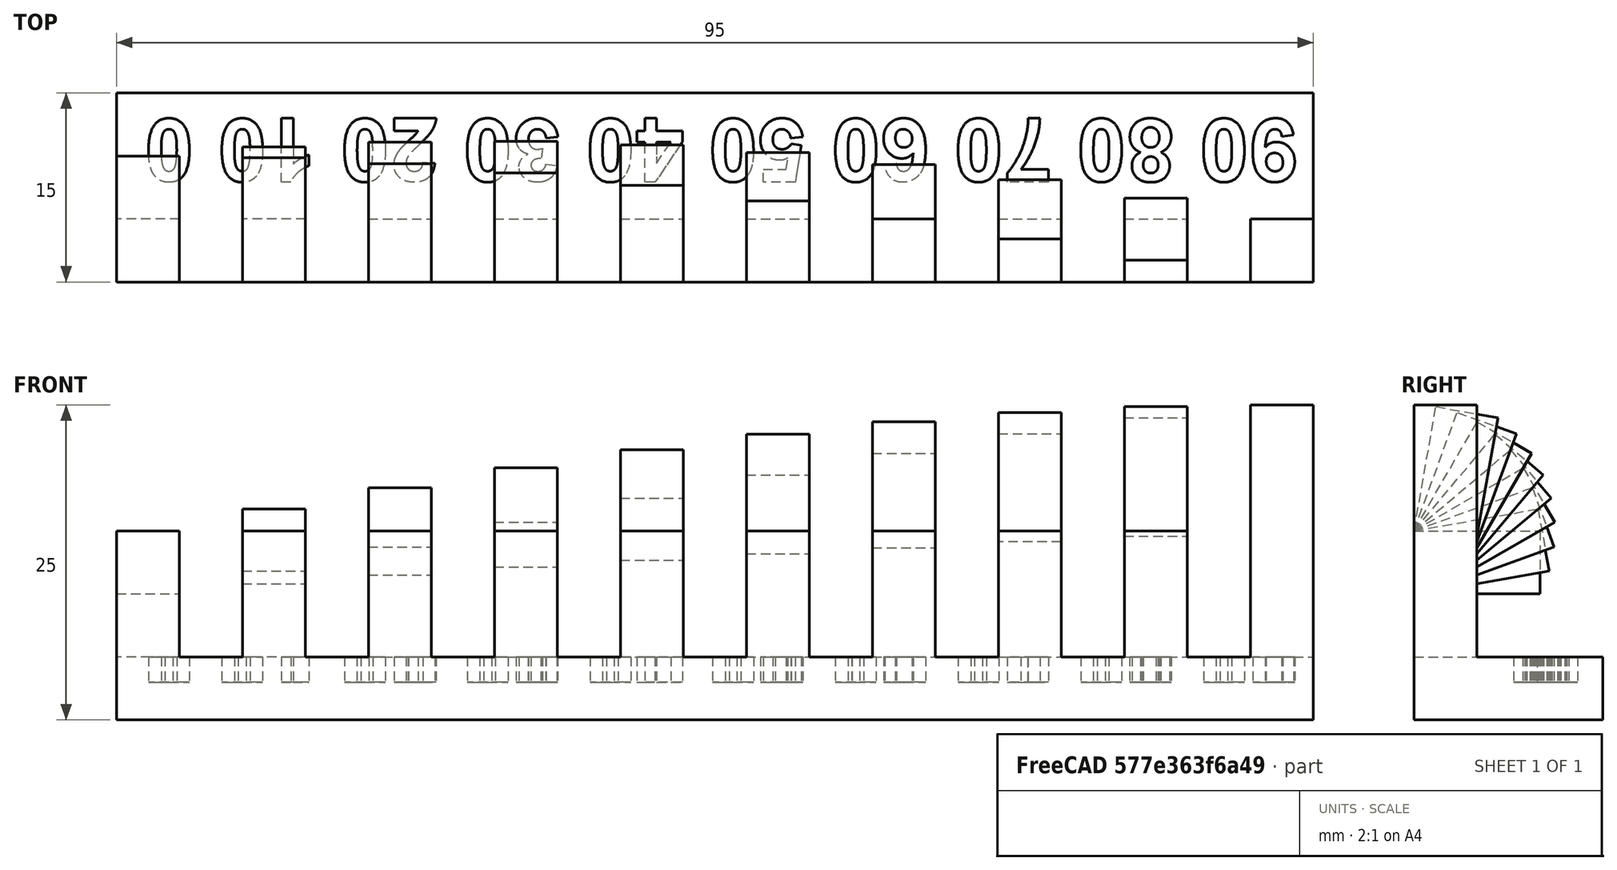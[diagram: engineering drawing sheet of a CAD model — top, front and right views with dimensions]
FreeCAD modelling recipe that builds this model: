
FCSTD DOCUMENT  (FreeCAD 0.18.3R)
Label: angle
License: All rights reserved
LicenseURL: http://en.wikipedia.org/wiki/All_rights_reserved
objects: Part::Box×20, Part::Fuse×8, Part::MultiFuse×2, Part::Part2DObjectPython×1, Part::Extrusion×1, Part::Cut×1
note: 33 computed .brp shape members not serialized (recipe doc carries the construction recipe); baked Part::Feature solids carry a one-line shape summary decoded from their .brp

FEATURE [Part::Box] Box  label="0"
  AttacherType = Attacher::AttachEngine3D
  Height = 20
  Length = 5
  Placement = pos=(0,0,-5) rot=(0,0,1;0rad)
  Width = 5
FEATURE [Part::Box] Box001  label="20 front"
  AttacherType = Attacher::AttachEngine3D
  Height = 10
  Length = 5
  Placement = pos=(-20,0,5) rot=(-1,0,0;0.349066rad)
  Width = 5
FEATURE [Part::Box] Box002  label="10 front"
  AttacherType = Attacher::AttachEngine3D
  Height = 10
  Length = 5
  Placement = pos=(-10,0,5) rot=(-1,0,0;0.174533rad)
  Width = 5
FEATURE [Part::Box] Box003  label="30 front"
  AttacherType = Attacher::AttachEngine3D
  Height = 10
  Length = 5
  Placement = pos=(-30,0,5) rot=(-1,0,0;0.523599rad)
  Width = 5
FEATURE [Part::Box] Box004  label="40 front"
  AttacherType = Attacher::AttachEngine3D
  Height = 10
  Length = 5
  Placement = pos=(-40,0,5) rot=(-1,0,0;0.698132rad)
  Width = 5
FEATURE [Part::Box] Box005  label="50 front"
  AttacherType = Attacher::AttachEngine3D
  Height = 10
  Length = 5
  Placement = pos=(-50,0,5) rot=(-1,0,0;0.872665rad)
  Width = 5
FEATURE [Part::Box] Box006  label="60 front"
  AttacherType = Attacher::AttachEngine3D
  Height = 10
  Length = 5
  Placement = pos=(-60,0,5) rot=(-1,0,0;1.0472rad)
  Width = 5
FEATURE [Part::Box] Box007  label="70 front"
  AttacherType = Attacher::AttachEngine3D
  Height = 10
  Length = 5
  Placement = pos=(-70,0,5) rot=(-1,0,0;1.22173rad)
  Width = 5
FEATURE [Part::Box] Box008  label="80 front"
  AttacherType = Attacher::AttachEngine3D
  Height = 10
  Length = 5
  Placement = pos=(-80,0,5) rot=(1,0,0;-1.39626rad)
  Width = 5
FEATURE [Part::Box] Box009  label="90 front"
  AttacherType = Attacher::AttachEngine3D
  Height = 10
  Length = 5
  Placement = pos=(-90,0,5) rot=(-1,0,0;1.5708rad)
  Width = 5
FEATURE [Part::Box] Box010  label="base"
  AttacherType = Attacher::AttachEngine3D
  Height = 5
  Length = 95
  Placement = pos=(-90,0,-10) rot=(0,0,1;0rad)
  Width = 15
FEATURE [Part::Box] Box011  label="40 back"
  AttacherType = Attacher::AttachEngine3D
  Height = 15
  Length = 5
  Placement = pos=(-40,0,-10) rot=(0,0,1;0rad)
  Width = 5
FEATURE [Part::Fuse] Fusion  label="40"
  Base = -> Box004
  Tool = -> Box011
FEATURE [Part::Box] Box012  label="30 back"
  AttacherType = Attacher::AttachEngine3D
  Height = 15
  Length = 5
  Placement = pos=(-30,0,-10) rot=(0,0,1;0rad)
  Width = 5
FEATURE [Part::Fuse] Fusion001  label="30"
  Base = -> Box003
  Tool = -> Box012
FEATURE [Part::Box] Box013  label="50 back"
  AttacherType = Attacher::AttachEngine3D
  Height = 15
  Length = 5
  Placement = pos=(-50,0,-10) rot=(0,0,1;0rad)
  Width = 5
FEATURE [Part::Fuse] Fusion002  label="50"
  Base = -> Box005
  Tool = -> Box013
FEATURE [Part::Box] Box014  label="20 back"
  AttacherType = Attacher::AttachEngine3D
  Height = 15
  Length = 5
  Placement = pos=(-20,0,-10) rot=(0,0,1;0rad)
  Width = 5
FEATURE [Part::MultiFuse] Fusion003  label="20"
  Shapes = -> [Box014,Box001]
FEATURE [Part::Box] Box015  label="10 back"
  AttacherType = Attacher::AttachEngine3D
  Height = 15
  Length = 5
  Placement = pos=(-10,0,-10) rot=(0,0,1;0rad)
  Width = 5
FEATURE [Part::Fuse] Fusion004  label="10"
  Base = -> Box002
  Tool = -> Box015
FEATURE [Part::Part2DObjectPython] ShapeString  # Draft 2D object (typed FeaturePython)
  FontFile = <userpath>/git/aws2/bin/fonts/Arial Bold.ttf
  Placement = pos=(3.75,13,-5) rot=(0,0,1;3.14159rad)
  Size = 5.35
  String = 90 80 70 60 50 40 30 20 10 0
  Support = -> [Box010]
  Tracking = 0
FEATURE [Part::Extrusion] Extrude
  Base = -> ShapeString
  Dir = (0,0,1)
  DirMode = 2
  FaceMakerClass = Part::FaceMakerBullseye
  LengthFwd = -2
  LengthRev = 0
  Solid = false
  Symmetric = false
FEATURE [Part::Cut] Cut
  Base = -> Box010
  Tool = -> Extrude
FEATURE [Part::Box] Box016  label="60 back"
  AttacherType = Attacher::AttachEngine3D
  Height = 15
  Length = 5
  Placement = pos=(-60,0,-10) rot=(0,0,1;0rad)
  Width = 5
FEATURE [Part::Fuse] Fusion005  label="60"
  Base = -> Box006
  Tool = -> Box016
FEATURE [Part::Box] Box017  label="70 back"
  AttacherType = Attacher::AttachEngine3D
  Height = 15
  Length = 5
  Placement = pos=(-70,0,-10) rot=(0,0,1;0rad)
  Width = 5
FEATURE [Part::Fuse] Fusion006  label="70"
  Base = -> Box007
  Tool = -> Box017
FEATURE [Part::Box] Box018  label="80 back"
  AttacherType = Attacher::AttachEngine3D
  Height = 15
  Length = 5
  Placement = pos=(-80,0,-10) rot=(0,0,1;0rad)
  Width = 5
FEATURE [Part::Fuse] Fusion007  label="80"
  Base = -> Box008
  Tool = -> Box018
FEATURE [Part::Box] Box019  label="90 back"
  AttacherType = Attacher::AttachEngine3D
  Height = 15
  Length = 5
  Placement = pos=(-90,0,-10) rot=(0,0,1;0rad)
  Width = 5
FEATURE [Part::Fuse] Fusion008  label="90"
  Base = -> Box009
  Tool = -> Box019
FEATURE [Part::MultiFuse] Fusion009  label="angles"
  Shapes = -> [Box,Fusion005,Fusion004,Fusion002,Fusion,Fusion001,Fusion003,Fusion006,Cut,Fusion007,Fusion008]
